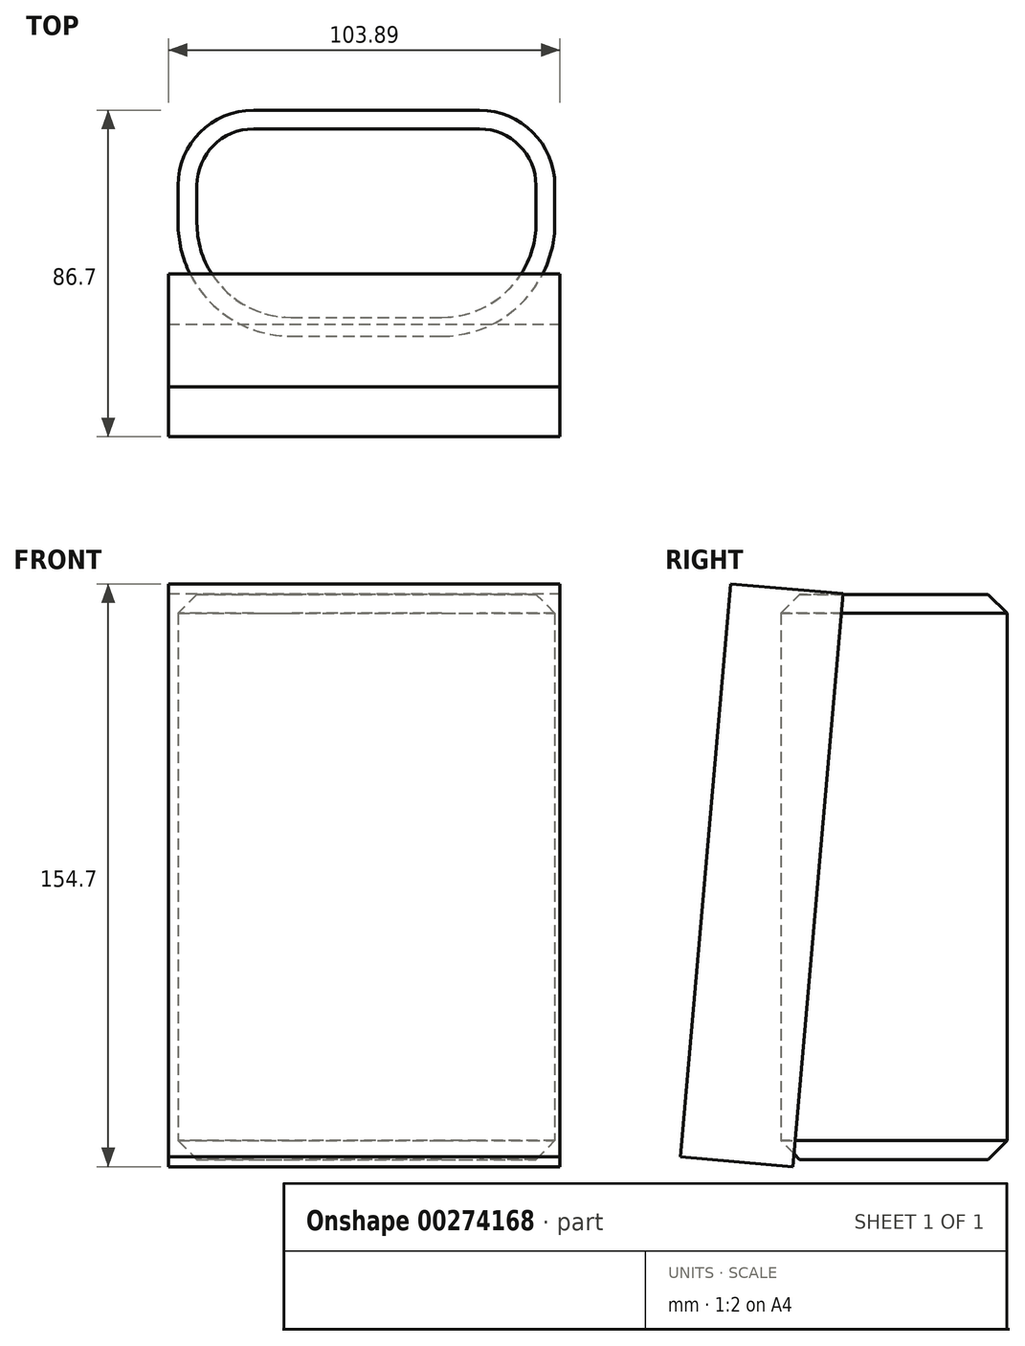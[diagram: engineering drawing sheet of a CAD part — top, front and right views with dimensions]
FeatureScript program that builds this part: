
annotation { "Feature Type Name" : "Feature", "Feature Type Description" : "" }
export const myFeature = defineFeature(function(context is Context, id is Id, definition is map)
    precondition{}
    {
        {
            var Q0;
            Q0=qCreatedBy(makeId("Front.planeOp"),FACE);
            var sketch = newSketch(context, id + "F0", { "sketchPlane" : qUnion([Q0])});
            skLineSegment(sketch, "E0.bottom", {"start": v(-50.8, 75.12) * mm, "end": v(49.2, 75.12) * mm});
            skLineSegment(sketch, "E0.top", {"start": v(-50.8, -74.88) * mm, "end": v(49.2, -74.88) * mm});
            skLineSegment(sketch, "E0.left", {"start": v(-50.8, 75.12) * mm, "end": v(-50.8, -74.88) * mm});
            skLineSegment(sketch, "E0.right", {"start": v(49.2, 75.12) * mm, "end": v(49.2, -74.88) * mm});
            skSolve(sketch);
        }
        {
            var Q0;
            Q0=makeQuery(id+"F0.imprint","IMPRINT",FACE,{"disambiguationData":[TD([[makeQuery(id+"F0.imprint","IMPRINT",EDGE,{"derivedFrom":sQuery(id+"F0.wireOp",EDGE,"E0.bottom")}),-1.0]])]});
            extrude(context, id + "F1", {"entities" : qUnion([Q0]), "depth" : 60 * mm});
        }
        {
            var Q0;
            Q0=makeQuery(id+"F1.opExtrude","CAP_EDGE",EDGE,{"disambiguationData":[OSD([sQuery(id+"F0.wireOp",EDGE,"E0.left")])],"isStart":true});
            var Q1;
            Q1=makeQuery(id+"F1.opExtrude","CAP_EDGE",EDGE,{"disambiguationData":[OSD([sQuery(id+"F0.wireOp",EDGE,"E0.right")])],"isStart":true});
            fillet(context, id + "F2", {"entities" : qUnion([Q0, Q1]), "radius" : 20 * mm, "tangentPropagation" : true, "allowEdgeOverflow" : false});
        }
        {
            var Q0;
            Q0=makeQuery(id+"F1.opExtrude","CAP_EDGE",EDGE,{"disambiguationData":[OSD([sQuery(id+"F0.wireOp",EDGE,"E0.right")])],"isStart":false});
            var Q1;
            Q1=makeQuery(id+"F1.opExtrude","CAP_EDGE",EDGE,{"disambiguationData":[OSD([sQuery(id+"F0.wireOp",EDGE,"E0.left")])],"isStart":false});
            fillet(context, id + "F3", {"entities" : qUnion([Q0, Q1]), "radius" : 30 * mm, "tangentPropagation" : true, "allowEdgeOverflow" : false});
        }
        {
            var Q0;
            Q0=makeQuery(id+"F1.opExtrude","SWEPT_FACE",FACE,{"disambiguationData":[OSD([sQuery(id+"F0.wireOp",EDGE,"E0.top")])]});
            var Q1;
            Q1=makeQuery(id+"F1.opExtrude","SWEPT_FACE",FACE,{"disambiguationData":[OSD([sQuery(id+"F0.wireOp",EDGE,"E0.bottom")])]});
            chamfer(context, id + "F4", {"entities" : qUnion([Q0, Q1]), "width" : 5 * mm, "tangentPropagation" : true});
        }
        {
            var Q0;
            Q0=qCreatedBy(makeId("Front.planeOp"),FACE);
            var sketch = newSketch(context, id + "F5", { "sketchPlane" : qUnion([Q0])});
            skLineSegment(sketch, "E1.bottom", {"start": v(-53.36, 75.52) * mm, "end": v(50.53, 75.52) * mm});
            skLineSegment(sketch, "E1.top", {"start": v(-53.36, -77.14) * mm, "end": v(50.53, -77.14) * mm});
            skLineSegment(sketch, "E1.left", {"start": v(-53.36, 75.52) * mm, "end": v(-53.36, -77.14) * mm});
            skLineSegment(sketch, "E1.right", {"start": v(50.53, 75.52) * mm, "end": v(50.53, -77.14) * mm});
            skSolve(sketch);
        }
        {
            var Q0;
            Q0=makeQuery(id+"F5.imprint","IMPRINT",FACE,{"disambiguationData":[TD([[makeQuery(id+"F5.imprint","IMPRINT",EDGE,{"derivedFrom":sQuery(id+"F5.wireOp",EDGE,"E1.bottom")}),-1.0]])]});
            extrude(context, id + "F6", {"entities" : qUnion([Q0]), "depth" : 30 * mm});
        }
        {
            var Q0;
            Q0=makeQuery(id+"F6.opExtrude","SWEPT_BODY",BODY,{"disambiguationData":[OSD([sQuery(id+"F5.wireOp",EDGE,"E1.bottom"),sQuery(id+"F5.wireOp",EDGE,"E1.top"),sQuery(id+"F5.wireOp",EDGE,"E1.left"),sQuery(id+"F5.wireOp",EDGE,"E1.right")])]});
            var Q1;
            Q1=makeQuery(id+"F6.opExtrude","CAP_EDGE",EDGE,{"disambiguationData":[OSD([sQuery(id+"F5.wireOp",EDGE,"E1.top")])],"isStart":true});
            transform(context, id + "F7", {"entities" : qUnion([Q0]), "transformType" : TransformType.ROTATION, "transformAxis" : qUnion([Q1]), "angle" : 10 * degree, "makeCopy" : false});
        }
        {
            var Q0;
            Q0=makeQuery(id+"F6.opExtrude","SWEPT_BODY",BODY,{"disambiguationData":[OSD([sQuery(id+"F5.wireOp",EDGE,"E1.bottom"),sQuery(id+"F5.wireOp",EDGE,"E1.top"),sQuery(id+"F5.wireOp",EDGE,"E1.left"),sQuery(id+"F5.wireOp",EDGE,"E1.right")])]});
            var Q1;
            Q1=makeQuery(id+"F6.opExtrude","CAP_EDGE",EDGE,{"disambiguationData":[OSD([sQuery(id+"F5.wireOp",EDGE,"E1.bottom")])],"isStart":true});
            transform(context, id + "F8", {"entities" : qUnion([Q0]), "transformType" : TransformType.ROTATION, "transformAxis" : qUnion([Q1]), "angle" : 15 * degree, "oppositeDirection" : true, "makeCopy" : false});
        }
        {
            var Q0;
            Q0=makeQuery(id+"F6.opExtrude","SWEPT_BODY",BODY,{"disambiguationData":[OSD([sQuery(id+"F5.wireOp",EDGE,"E1.bottom"),sQuery(id+"F5.wireOp",EDGE,"E1.top"),sQuery(id+"F5.wireOp",EDGE,"E1.left"),sQuery(id+"F5.wireOp",EDGE,"E1.right")])]});
            transform(context, id + "F9", {"entities" : qUnion([Q0]), "transformType" : TransformType.TRANSLATION_3D, "dx" : 0 * mm, "dy" : -17 * mm, "dz" : 0 * mm, "makeCopy" : false});
        }
        {
            var Q0;
            Q0=makeQuery(id+"F6.opExtrude","SWEPT_BODY",BODY,{"disambiguationData":[OSD([sQuery(id+"F5.wireOp",EDGE,"E1.bottom"),sQuery(id+"F5.wireOp",EDGE,"E1.top"),sQuery(id+"F5.wireOp",EDGE,"E1.left"),sQuery(id+"F5.wireOp",EDGE,"E1.right")])]});
            transform(context, id + "F10", {"entities" : qUnion([Q0]), "transformType" : TransformType.TRANSLATION_3D, "dx" : 0 * mm, "dy" : 0 * mm, "dz" : 2.1 * mm, "makeCopy" : false});
        }
    });
